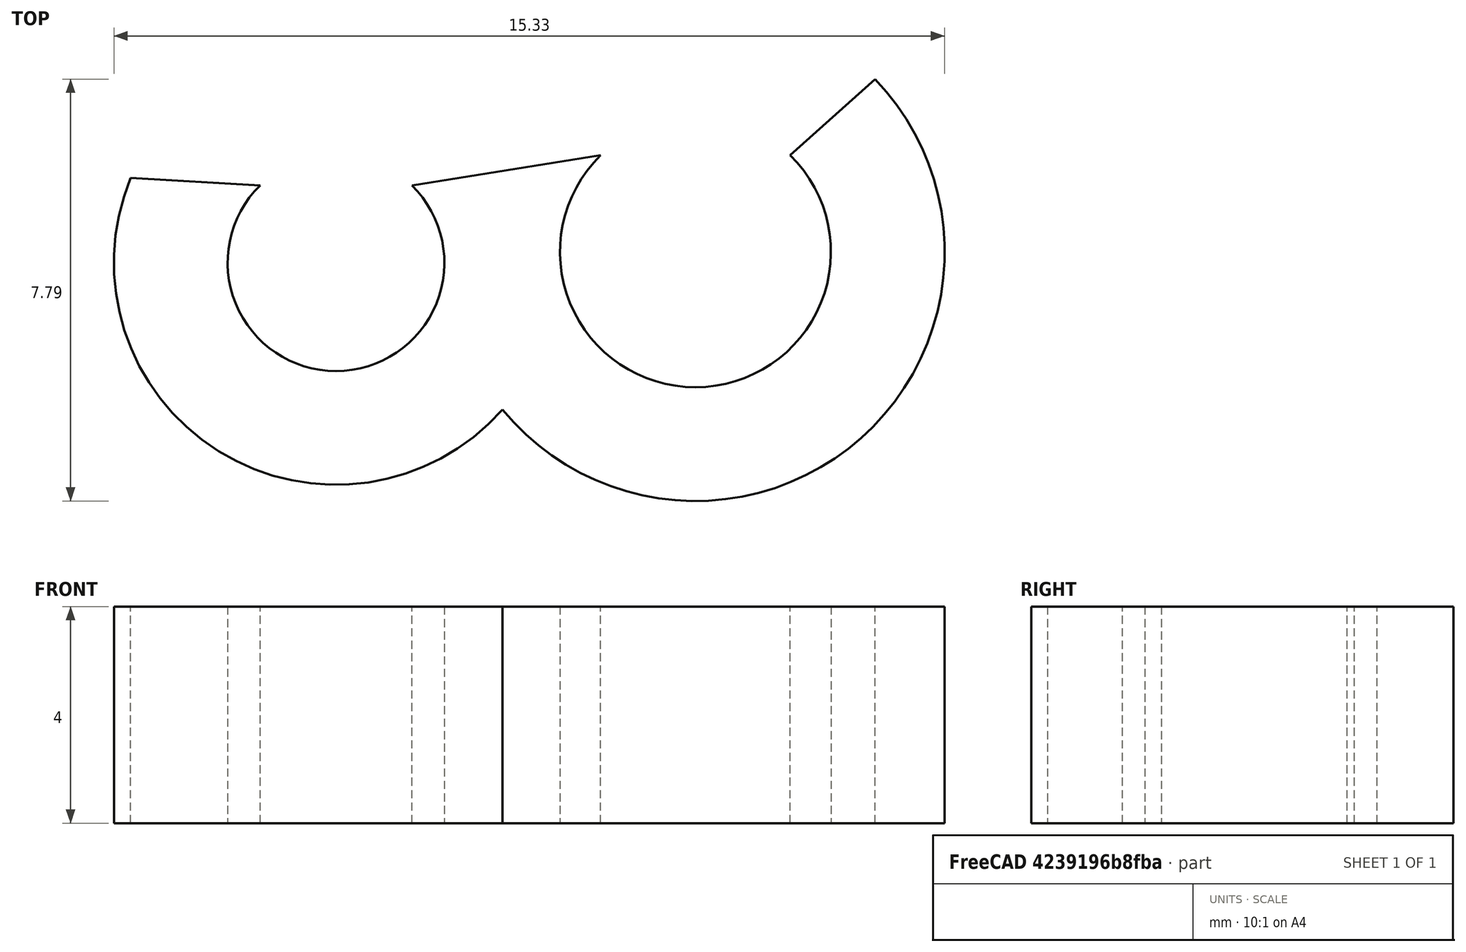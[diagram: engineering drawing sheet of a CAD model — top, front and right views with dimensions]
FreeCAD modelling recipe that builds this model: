
FCSTD DOCUMENT  (FreeCAD 0.17R13522 (Git))
Label: QiGan-jwei-2.0
License: All rights reserved
LicenseURL: http://en.wikipedia.org/wiki/All_rights_reserved
objects: Sketcher::SketchObject×1, PartDesign::Pad×1, PartDesign::Body×1
note: 4 computed .brp shape members not serialized (recipe doc carries the construction recipe); baked Part::Feature solids carry a one-line shape summary decoded from their .brp

FEATURE [Sketcher::SketchObject] Sketch
  MapMode = 5
  Support = -> [XY_Plane]
  sketch-geometry (7):
    g0: ArcOfCircle CenterX=0 CenterY=1 CenterZ=0 NormalX=0 NormalY=0 NormalZ=1 AngleXU=0 Radius=2 StartAngle=2.34619 EndAngle=7.07858
    g1: ArcOfCircle CenterX=6.63325 CenterY=1.2 CenterZ=0 NormalX=0 NormalY=0 NormalZ=1 AngleXU=0 Radius=2.5 StartAngle=2.34619 EndAngle=7.07858
    g2: ArcOfCircle CenterX=6.63325 CenterY=1.2 CenterZ=0 NormalX=0 NormalY=0 NormalZ=1 AngleXU=0 Radius=4.6 StartAngle=3.8275 EndAngle=7.04979
    g3: ArcOfCircle CenterX=0 CenterY=1 CenterZ=0 NormalX=0 NormalY=0 NormalZ=1 AngleXU=0 Radius=4.1 StartAngle=2.74988 EndAngle=5.55992
    g4: LineSegment StartX=-3.78946 StartY=2.56525 StartZ=0 EndX=-1.4 EndY=2.42829 EndZ=0
    g5: LineSegment StartX=1.4 StartY=2.42829 StartZ=0 EndX=4.88325 EndY=2.98536 EndZ=0
    g6: LineSegment StartX=8.38325 StartY=2.98536 StartZ=0 EndX=9.94651 EndY=4.39098 EndZ=0
  constraints (21):
    c: Radius(g0) = 2
    c: Distance(g0,g0) = 2.8
    c: Radius(g1) = 2.5
    c: Distance(g1,g1) = 3.5
    c: DistanceY(g-1,g1) = 1.2
    c: Coincident(g2,g1)
    c: Radius(g2) = 4.6
    c: Horizontal(g0,g0)
    c: Radius(g3) = 4.1
    c: Horizontal(g1,g1)
    c: Coincident(g3,g0)
    c: PointOnObject(g0,g-2)
    c: Distance(g-1,g0) = 1
    c: PointOnObject(g2,g3)
    c: Coincident(g3,g2)
    c: Coincident(g4,g3)
    c: Coincident(g4,g0)
    c: Coincident(g5,g0)
    c: Coincident(g5,g1)
    c: Coincident(g6,g1)
    c: Coincident(g6,g2)
FEATURE [PartDesign::Pad] Pad
  Length = 4
  Length2 = 100
  Profile = -> Sketch
  Type = 0
FEATURE [PartDesign::Body] Body
  Group = -> [Sketch,Pad]
  Origin = -> Origin
  Tip = -> Pad
